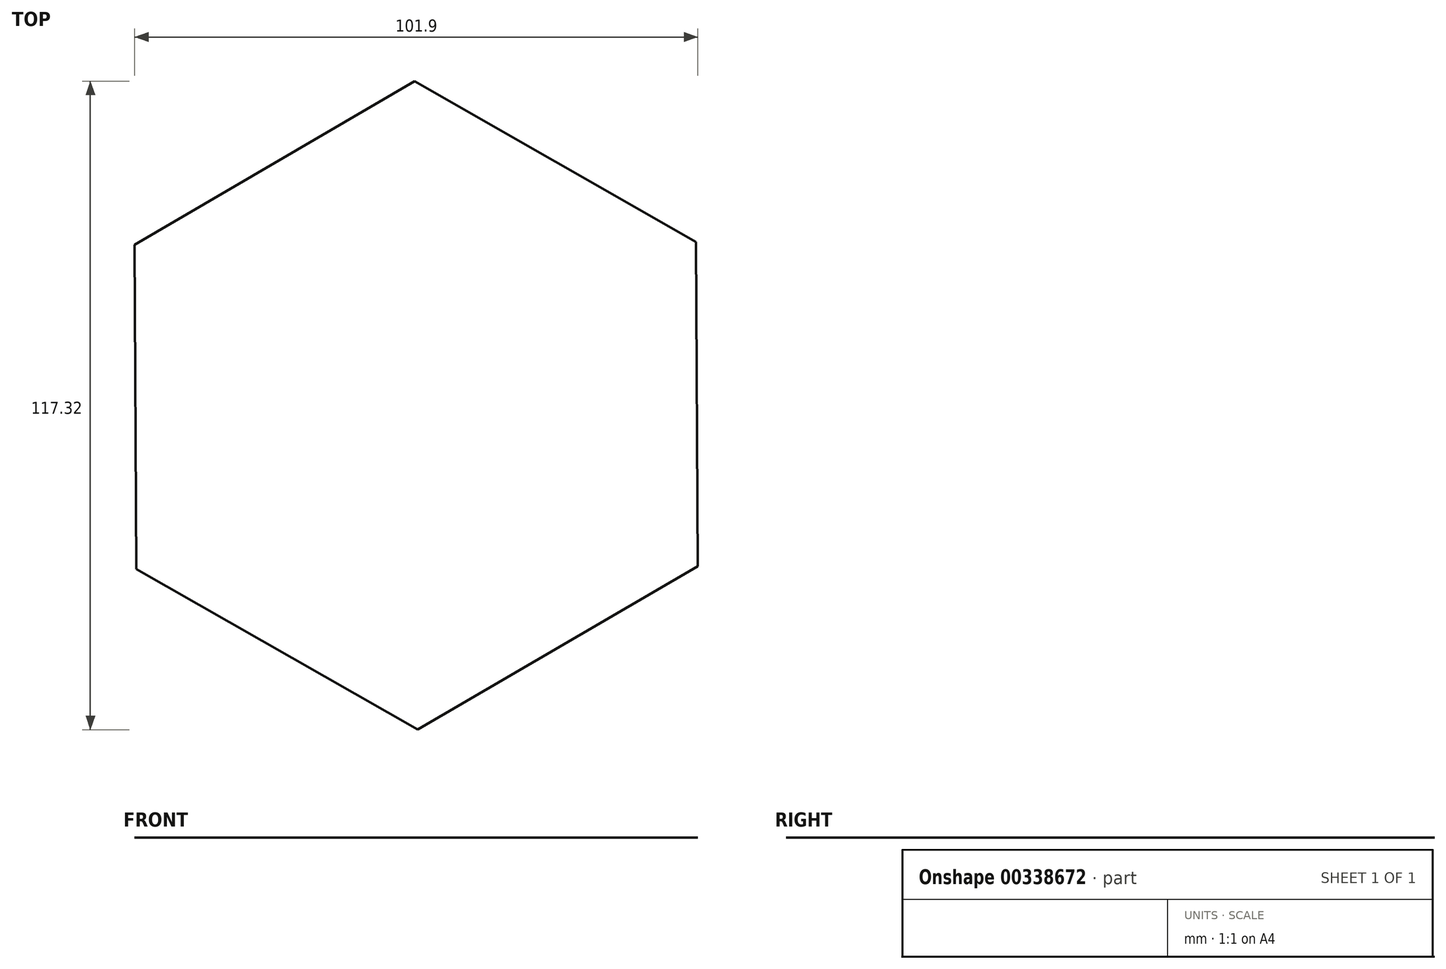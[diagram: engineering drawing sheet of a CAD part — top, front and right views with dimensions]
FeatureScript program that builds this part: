
annotation { "Feature Type Name" : "Feature", "Feature Type Description" : "" }
export const myFeature = defineFeature(function(context is Context, id is Id, definition is map)
    precondition{}
    {
        {
            var Q0;
            Q0=qCreatedBy(makeId("Top.planeOp"),FACE);
            var sketch = newSketch(context, id + "F0", { "sketchPlane" : qUnion([Q0])});
            skPoint(sketch, "E0.middle", {"position": v(0, 0) * mm});
            skCircle(sketch, "E1.cCircle", {"center": v(0, 0) * mm, "radius": 50.8 * mm, "construction": true});
            skLineSegment(sketch, "E1.0", {"start": v(-50.95, 29.07) * mm, "end": v(-0.3, 58.66) * mm});
            skLineSegment(sketch, "E1.1", {"start": v(-0.3, 58.66) * mm, "end": v(50.65, 29.59) * mm});
            skLineSegment(sketch, "E1.2", {"start": v(50.65, 29.59) * mm, "end": v(50.95, -29.07) * mm});
            skLineSegment(sketch, "E1.3", {"start": v(50.95, -29.07) * mm, "end": v(0.3, -58.66) * mm});
            skLineSegment(sketch, "E1.4", {"start": v(0.3, -58.66) * mm, "end": v(-50.65, -29.59) * mm});
            skLineSegment(sketch, "E1.5", {"start": v(-50.65, -29.59) * mm, "end": v(-50.95, 29.07) * mm});
            skPoint(sketch, "E1.0.midPoint", {"position": v(-25.62, 43.86) * mm});
            skSolve(sketch);
        }
        {
            var Q0;
            Q0=makeQuery(id+"F0.imprint","IMPRINT",FACE,{"disambiguationData":[TD([[makeQuery(id+"F0.imprint","IMPRINT",EDGE,{"derivedFrom":sQuery(id+"F0.wireOp",EDGE,"E1.0")}),-1.0]])]});
            extrude(context, id + "F1", {"entities" : qUnion([Q0]), "depth" : 1 / 203.2 * mm});
        }
    });
